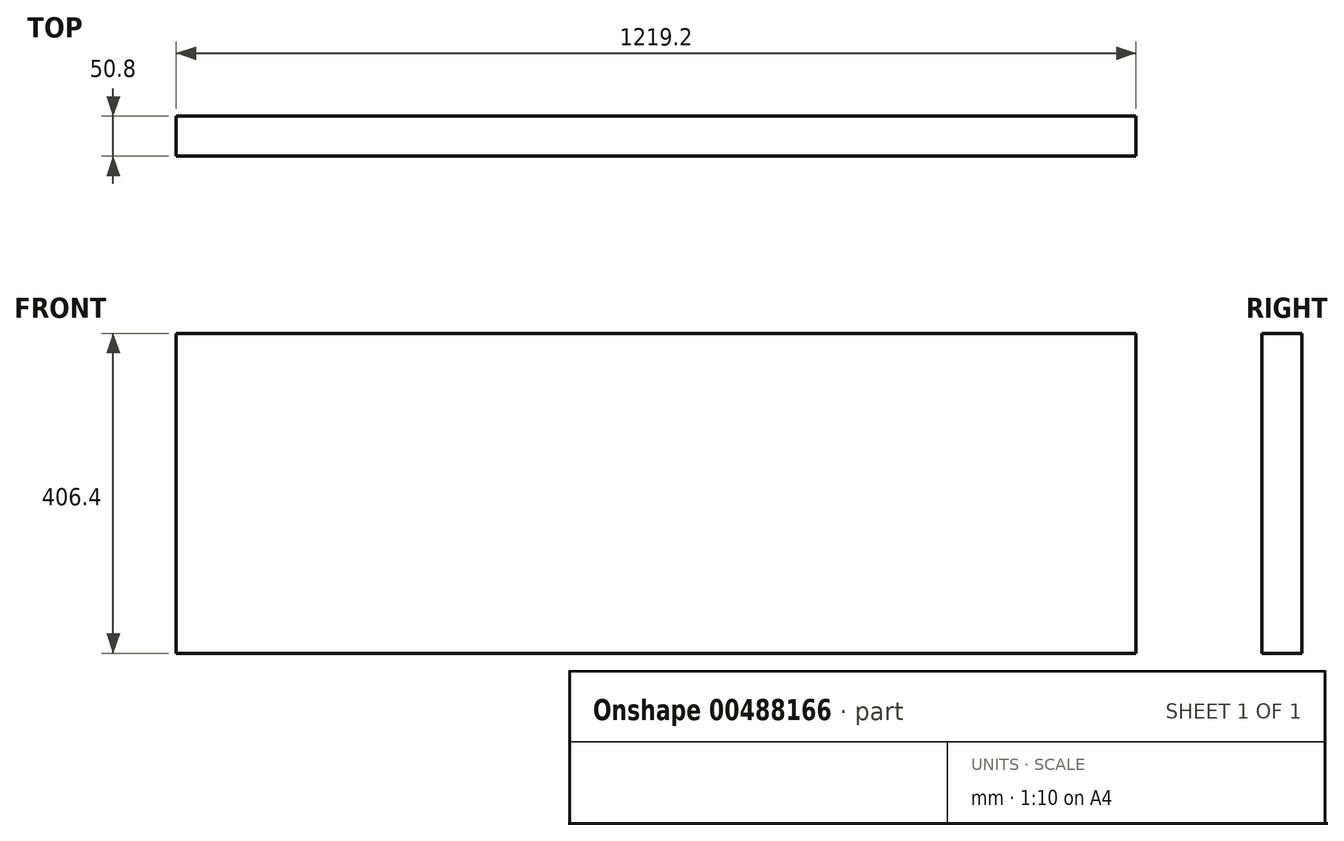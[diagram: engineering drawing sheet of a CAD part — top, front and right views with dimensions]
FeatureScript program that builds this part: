
annotation { "Feature Type Name" : "Feature", "Feature Type Description" : "" }
export const myFeature = defineFeature(function(context is Context, id is Id, definition is map)
    precondition{}
    {
        {
            var Q0;
            Q0=qCreatedBy(makeId("Front.planeOp"),FACE);
            var sketch = newSketch(context, id + "F0", { "sketchPlane" : qUnion([Q0])});
            skLineSegment(sketch, "E0", {"start": v(0, 0) * mm, "end": v(1219.2, 0) * mm});
            skLineSegment(sketch, "E1", {"start": v(1219.2, 0) * mm, "end": v(1219.2, 406.4) * mm});
            skLineSegment(sketch, "E2", {"start": v(1219.2, 406.4) * mm, "end": v(0, 406.4) * mm});
            skLineSegment(sketch, "E3", {"start": v(0, 406.4) * mm, "end": v(0, 0) * mm});
            skSolve(sketch);
        }
        {
            var Q0;
            Q0=makeQuery(id+"F0.imprint","IMPRINT",FACE,{"disambiguationData":[TD([[makeQuery(id+"F0.imprint","IMPRINT",EDGE,{"derivedFrom":sQuery(id+"F0.wireOp",EDGE,"E0")}),1.0]])]});
            extrude(context, id + "F1", {"entities" : qUnion([Q0]), "depth" : 50.8 * mm, "offsetDistance" : 25.4 * mm});
        }
    });
